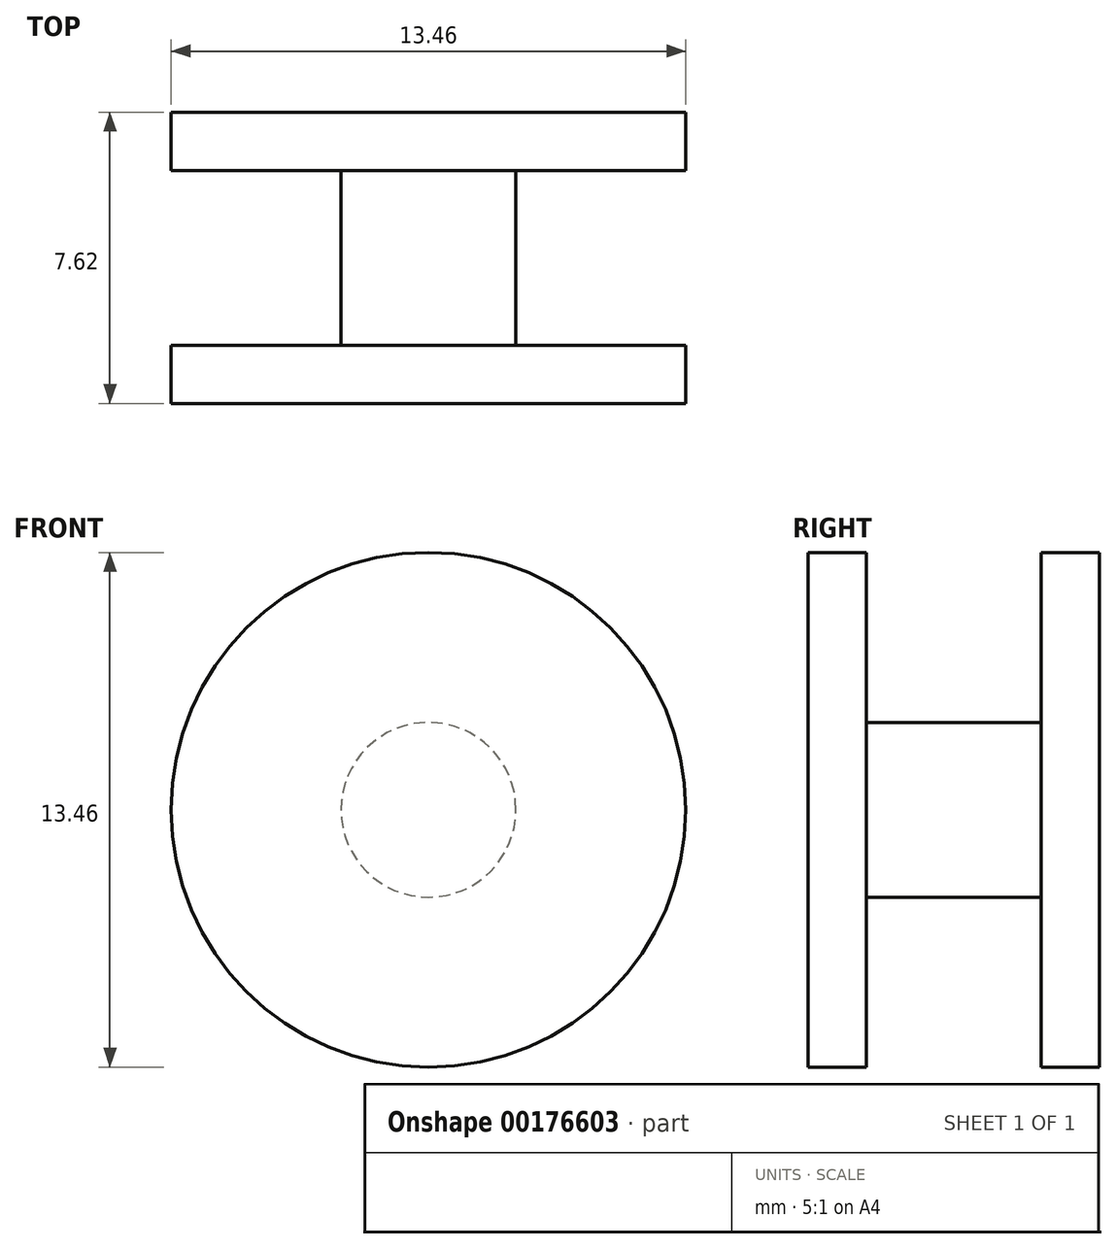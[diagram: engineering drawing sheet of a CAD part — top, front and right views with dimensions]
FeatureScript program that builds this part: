
annotation { "Feature Type Name" : "Feature", "Feature Type Description" : "" }
export const myFeature = defineFeature(function(context is Context, id is Id, definition is map)
    precondition{}
    {
        {
            var Q0;
            Q0=qCreatedBy(makeId("Front.planeOp"),FACE);
            var sketch = newSketch(context, id + "F0", { "sketchPlane" : qUnion([Q0])});
            skCircle(sketch, "E0", {"center": v(0, 0) * mm, "radius": 2.29 * mm});
            skSolve(sketch);
        }
        {
            var Q0;
            Q0 = qSketchRegion(id + "F0", true);
            extrude(context, id + "F1", {"entities" : qUnion([Q0]), "depth" : 2.3 * mm});
        }
        {
            var Q0;
            Q0=makeQuery(id+"F1.opExtrude","CAP_FACE",FACE,{"disambiguationData":[OSD([sQuery(id+"F0.wireOp",EDGE,"E0")])],"isStart":true});
            extrude(context, id + "F2", {"entities" : qUnion([Q0]), "operationType" : NewBodyOperationType.ADD, "depth" : 2.3 * mm});
        }
        {
            var Q0;
            Q0=makeQuery(id+"F1.opExtrude","CAP_FACE",FACE,{"disambiguationData":[OSD([sQuery(id+"F0.wireOp",EDGE,"E0")])],"isStart":false});
            var sketch = newSketch(context, id + "F3", { "sketchPlane" : qUnion([Q0])});
            skCircle(sketch, "E1", {"center": v(0, 0) * mm, "radius": 6.73 * mm});
            skSolve(sketch);
        }
        {
            var Q0;
            Q0 = qSketchRegion(id + "F3", true);
            extrude(context, id + "F4", {"entities" : qUnion([Q0]), "operationType" : NewBodyOperationType.ADD, "depth" : 1.52 * mm});
        }
        {
            var Q0;
            Q0=makeQuery(id+"F2.opExtrude","CAP_FACE",FACE,{"disambiguationData":[OSD([sQuery(id+"F0.wireOp",EDGE,"E0")])],"isStart":false});
            var sketch = newSketch(context, id + "F5", { "sketchPlane" : qUnion([Q0])});
            skCircle(sketch, "E2", {"center": v(0, 0) * mm, "radius": 6.73 * mm});
            skSolve(sketch);
        }
        {
            var Q0;
            Q0 = qSketchRegion(id + "F5", true);
            extrude(context, id + "F6", {"entities" : qUnion([Q0]), "operationType" : NewBodyOperationType.ADD, "depth" : 1.52 * mm});
        }
    });
